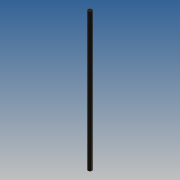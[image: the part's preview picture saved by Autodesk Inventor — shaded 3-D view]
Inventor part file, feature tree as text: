
AUTODESK INVENTOR PART (.ipt)
format: ipt  version: 2014 SP1 (Build 180222100, 222)  size: 123,904 bytes
history: native  units: in
note: dims shown in document units (in); Inventor stores cm internally (conversion verified against a paired STEP export)
features: sketch x8, extrude x6, plane x2
ambient origin geometry x8: Origin, YZ Plane, XZ Plane, XY Plane, X Axis, Y Axis, Z Axis, Center Point
bodies: Solid1 (feature_tree)
feature tree (16):
  extrude  "Extrusion1"  Depth=275.5906in TaperAngle=0.0deg
  extrude  "Extrusion2"  Depth=0.01in TaperAngle=0.0deg
  sketch  "Sketch3"  dims[d7=2.0in d8=3.0in]
  plane  "Work Plane1"
  extrude  "poleStandRadialRef"  Depth=3.0in
  sketch  "Sketch5"  dims[d12=12.0in d13=1.0in d14=0.0in]
  plane  "Work Plane2"
  extrude  "poleStandOffsetRef"  Depth=0.5in
  extrude  "eyeBoltHole"  Depth=1.0in TaperAngle=0.0deg
  extrude  "smallEyeBolt"  Depth=100.0in
  sketch  "Sketch1"  dims[d0=8.0in d1=275.5906in d2=0.0in]
  sketch  "Sketch2"  dims[d3=39.3701in d4=0.0in d5=0.01in d6=0.0in]
  sketch  "Sketch4"  dims[d9=0.01in d10=0.0in d11=0.5in]
  sketch  "Sketch6"  dims[d15=0.125in d16=100.0in]
  sketch  "Sketch7"  dims[d17=1.0in d18=0.0in]
  sketch  "Sketch8"
